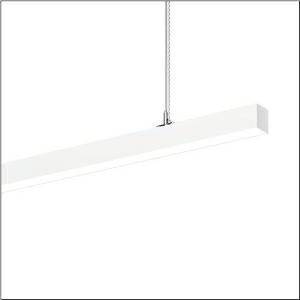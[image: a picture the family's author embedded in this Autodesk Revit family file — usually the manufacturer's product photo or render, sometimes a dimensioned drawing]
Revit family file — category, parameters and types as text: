
# Revit family: silica_r__21_51mx30da34wb_efde
name_source: partatom
category: Lighting Fixtures
units: mm (PartAtom-declared; Revit-internal decimal feet)

## family parameters
Cut with Voids When Loaded = No
Host = Face
Light Source = No
Part Type = Normal
Room Calculation Point = No
Round Connector Dimension = Use Diameter
Shared = No

## types (1)
- --- (1 x LED, 4210 lm, 27.7 W, 3000K)
    Apparent Load = 28 VA
    CIE Flux Codes = 47 79 96 57 100
    Color Rendering = 80
    Color Temperature = 3000K
    Default Elevation = 1800 mm
    Description = Silica® 21, office luminaire, primary optical cover: cover, of PMMA, opal, light emission: direct/indirect distribution, primary light characteristic: symmetric, installation type: suspended mounting, LED, rated luminous flux: 4.210lm, luminous efficacy: 152lm/W, light colour: 830, colour temperature: 3000K, control gear: DALI 2, with terminal, 3+2-pole, max. 2.5mm², mains connection: 220..240V, AC, 50/60Hz, rated input power: 27.7W, luminaire housing, of aluminium, traffic white (RAL 9016), length: 1.204mm, width: 53mm, height: 53mm, protection rating (complete): IP20, insulation class (complete): insulation class I (protective earthing), certification: CE, permissible operating ambient temperature: 0..+35°C, standard: EN 50419, packaging unit: 1 piece
    Height = 53 mm
    Lamp = 1 x LED
    Lamp Light Flux = 4210 lm
    Lamp Power = 27.7 W
    Lamp count = 1
    Length = 1204 mm
    Luminous efficacy = 152 lm/W
    Manufacturer = Siteco
    ModVariant = No
    Model = 51MX30DA34WB
    Mounting Place = Ceiling
    Mounting Type = Pendant
    Number of Poles = 1
    OnlyDefault = Yes
    Power Factor = 1
    Product Name = Silica® 21
    Product group = office luminaire | ceiling pendant
    ProductGroupID = 904
    Protection Class = Protection class I
    Protection Degree = IP 20
    RLX_Detail_Level = 1
    RLX_Emergency_Light_Flux = 0 lm
    RLX_Emergency_Type = 0
    RLX_Emergency_Type_DB = No
    RlxData = <blob elided: 20761 chars, md5=5b30d096>
    Socket = socket
    Standby Power = 0 W
    System Light Flux = 4210 lm
    System Power = 28 W
    Type Comments = factory setting: luminous flux: 100 % | dim-lin: 254 | 233 mA
    Type Image = l_1349023.jpg
    URL = http://relux.com
    VarID = @adj_117474
    Voltage = 0 V
    Weight = 0.00 kg
    Width = 53 mm

## geometry (parser evidence)
native form markers: Blend x4, Sweep x12
no freeform markers — native parametric forms only
